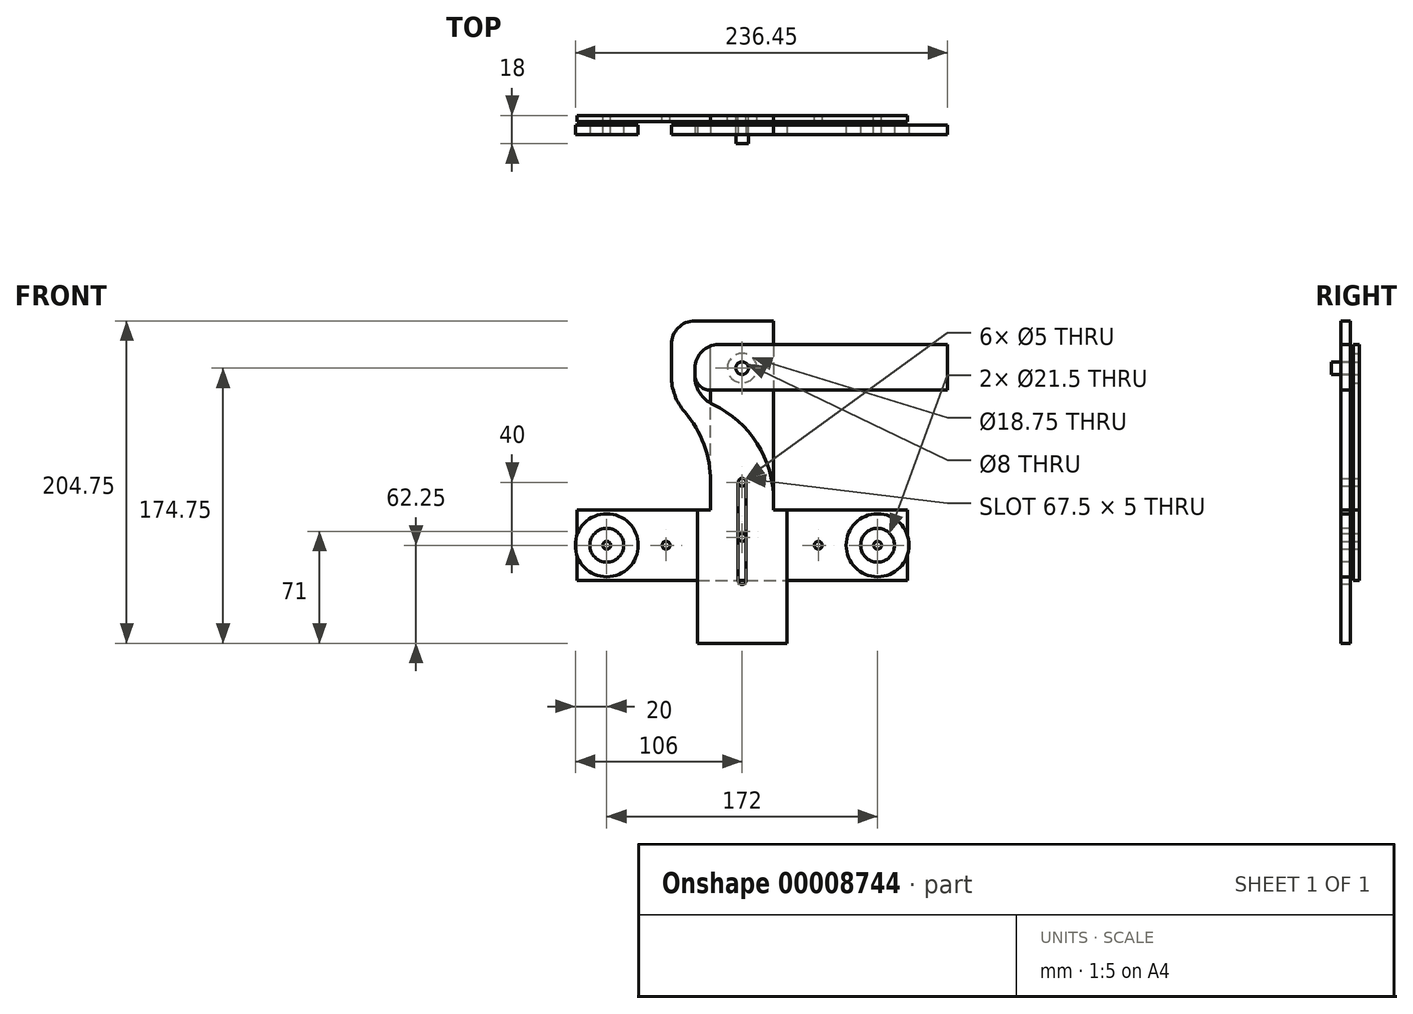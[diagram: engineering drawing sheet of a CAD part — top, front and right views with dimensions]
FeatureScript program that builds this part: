
annotation { "Feature Type Name" : "Feature", "Feature Type Description" : "" }
export const myFeature = defineFeature(function(context is Context, id is Id, definition is map)
    precondition{}
    {
        {
            var Q0;
            Q0=qCreatedBy(makeId("Front.planeOp"),FACE);
            var sketch = newSketch(context, id + "F0", { "sketchPlane" : qUnion([Q0])});
            skLineSegment(sketch, "E0", {"start": v(105, 22.5) * mm, "end": v(105, -22.5) * mm});
            skLineSegment(sketch, "E1", {"start": v(-20, 22.5) * mm, "end": v(-105, 22.5) * mm});
            skLineSegment(sketch, "E2", {"start": v(-105, -22.5) * mm, "end": v(-105, 22.5) * mm});
            skCircle(sketch, "E3", {"center": v(0, 40) * mm, "radius": 2.5 * mm});
            skLineSegment(sketch, "E4", {"start": v(-20, 112.5) * mm, "end": v(20, 112.5) * mm, "construction": true});
            skCircle(sketch, "E5", {"center": v(0, 112.5) * mm, "radius": 9.38 * mm});
            skLineSegment(sketch, "E6", {"start": v(-105, -22.5) * mm, "end": v(105, -22.5) * mm});
            skCircle(sketch, "E7", {"center": v(0, 5) * mm, "radius": 2.5 * mm});
            skCircle(sketch, "E8", {"center": v(-86, 0) * mm, "radius": 2.5 * mm});
            skCircle(sketch, "E9", {"center": v(86, 0) * mm, "radius": 2.5 * mm});
            skLineSegment(sketch, "E10", {"start": v(-20, 22.5) * mm, "end": v(20, 22.5) * mm, "construction": true});
            skLineSegment(sketch, "E11", {"start": v(0, 112.5) * mm, "end": v(0, -22.5) * mm, "construction": true});
            skLineSegment(sketch, "E12", {"start": v(-86, 0) * mm, "end": v(0, 0) * mm, "construction": true});
            skLineSegment(sketch, "E13", {"start": v(0, 0) * mm, "end": v(86, 0) * mm, "construction": true});
            skPoint(sketch, "E14", {"position": v(105, 0) * mm});
            skPoint(sketch, "E15", {"position": v(0, -22.5) * mm});
            skCircle(sketch, "E16", {"center": v(-48.35, 0) * mm, "radius": 20 * mm, "construction": true});
            skCircle(sketch, "E17", {"center": v(48.35, 0) * mm, "radius": 20 * mm, "construction": true});
            skCircle(sketch, "E18", {"center": v(-86, 0) * mm, "radius": 20 * mm, "construction": true});
            skCircle(sketch, "E19", {"center": v(86, 0) * mm, "radius": 20 * mm, "construction": true});
            skLineSegment(sketch, "E20", {"start": v(-20, 22.5) * mm, "end": v(-20, 127.5) * mm});
            skLineSegment(sketch, "E21", {"start": v(-20, 127.5) * mm, "end": v(20, 127.5) * mm});
            skLineSegment(sketch, "E22", {"start": v(20, 127.5) * mm, "end": v(20, 22.5) * mm});
            skLineSegment(sketch, "E23", {"start": v(20, 22.5) * mm, "end": v(105, 22.5) * mm});
            skCircle(sketch, "E24", {"center": v(-48.35, 0) * mm, "radius": 2.5 * mm});
            skCircle(sketch, "E25", {"center": v(48.35, 0) * mm, "radius": 2.5 * mm});
            skSolve(sketch);
        }
        {
            var Q0;
            Q0 = qSketchRegion(id + "F0", true);
            extrude(context, id + "F1", {"entities" : qUnion([Q0]), "depth" : 4 * mm});
        }
        {
            var Q0;
            Q0=makeQuery(id+"F1.opExtrude","CAP_FACE",FACE,{"disambiguationData":[OSD([sQuery(id+"F0.wireOp",EDGE,"E0"),sQuery(id+"F0.wireOp",EDGE,"b1bdffde-36e9-4f26-b447-62229c1635de"),sQuery(id+"F0.wireOp",EDGE,"6c009403-4b52-4c06-8701-ef34f8ef2d19"),sQuery(id+"F0.wireOp",EDGE,"f10999cf-903d-418b-98b1-c5591cbe51ed"),sQuery(id+"F0.wireOp",EDGE,"E1"),sQuery(id+"F0.wireOp",EDGE,"E2"),sQuery(id+"F0.wireOp",EDGE,"E3"),sQuery(id+"F0.wireOp",EDGE,"E5"),sQuery(id+"F0.wireOp",EDGE,"E6"),sQuery(id+"F0.wireOp",EDGE,"E7"),sQuery(id+"F0.wireOp",EDGE,"E8"),sQuery(id+"F0.wireOp",EDGE,"E9"),sQuery(id+"F0.wireOp",EDGE,"a64ca942-9197-43bc-8cf3-53473cfb3008"),sQuery(id+"F0.wireOp",EDGE,"94b97b06-c2ea-428e-ab4c-9c243ee04647"),sQuery(id+"F0.wireOp",EDGE,"e7d3e3b6-22b7-4308-8daa-f254cc9a82a0")])],"isStart":true});
            var sketch = newSketch(context, id + "F2", { "sketchPlane" : qUnion([Q0])});
            skCircle(sketch, "E26.0", {"center": v(0, 112.5) * mm, "radius": 4 * mm});
            skCircle(sketch, "E26.1", {"center": v(0, 40) * mm, "radius": 2.5 * mm});
            skCircle(sketch, "E26.2", {"center": v(0, 5) * mm, "radius": 2.5 * mm});
            skCircle(sketch, "E26.3", {"center": v(86, 0) * mm, "radius": 2.5 * mm});
            skCircle(sketch, "E26.4", {"center": v(-86, 0) * mm, "radius": 2.5 * mm});
            skSolve(sketch);
        }
        {
            var Q0;
            Q0 = qSketchRegion(id + "F2", true);
            extrude(context, id + "F3", {"entities" : qUnion([Q0]), "oppositeDirection" : true, "depth" : (4 * 3) * mm});
        }
        {
            var Q0;
            Q0=makeQuery(id+"F3.opExtrude","CAP_FACE",FACE,{"disambiguationData":[OSD([sQuery(id+"F2.wireOp",EDGE,"E26.0")])],"isStart":false});
            var sketch = newSketch(context, id + "F4", { "sketchPlane" : qUnion([Q0])});
            skCircle(sketch, "E27", {"center": v(-86, 0) * mm, "radius": 20 * mm});
            skCircle(sketch, "E28", {"center": v(86, 0) * mm, "radius": 20 * mm});
            skCircle(sketch, "E29", {"center": v(-86, 0) * mm, "radius": 10.75 * mm});
            skCircle(sketch, "E30", {"center": v(86, 0) * mm, "radius": 10.75 * mm});
            skSolve(sketch);
        }
        {
            var Q0;
            Q0 = qSketchRegion(id + "F4", true);
            extrude(context, id + "F5", {"entities" : qUnion([Q0]), "oppositeDirection" : true, "depth" : 6 * mm});
        }
        {
            var Q0;
            Q0=makeQuery(id+"F5.opExtrude","CAP_FACE",FACE,{"disambiguationData":[OSD([sQuery(id+"F4.wireOp",EDGE,"E27"),sQuery(id+"F4.wireOp",EDGE,"E29")])],"isStart":true});
            var sketch = newSketch(context, id + "F6", { "sketchPlane" : qUnion([Q0])});
            skArc(sketch, "E31", {"start": v(-2.5, -22.5) * mm, "mid": v(0, -25) * mm, "end": v(2.5, -22.5) * mm});
            skLineSegment(sketch, "E32", {"start": v(0, 129.3) * mm, "end": v(0, -22.5) * mm, "construction": true});
            skLineSegment(sketch, "E33", {"start": v(2.5, -22.5) * mm, "end": v(2.5, 40) * mm});
            skLineSegment(sketch, "E34", {"start": v(-2.5, -22.5) * mm, "end": v(-2.5, 40) * mm});
            skArc(sketch, "E35", {"start": v(2.5, 40) * mm, "mid": v(0, 42.5) * mm, "end": v(-2.5, 40) * mm});
            skLineSegment(sketch, "E36", {"start": v(-30, 142.5) * mm, "end": v(20, 142.5) * mm});
            skLineSegment(sketch, "E37", {"start": v(20, 142.5) * mm, "end": v(20, 127.5) * mm});
            skLineSegment(sketch, "E38", {"start": v(20, 127.5) * mm, "end": v(-15, 127.5) * mm});
            skArc(sketch, "E39.filletArc", {"start": v(-15, 127.5) * mm, "mid": v(-25.6, 123.1) * mm, "end": v(-30, 112.5) * mm});
            skArc(sketch, "E40.filletArc", {"start": v(-30, 142.5) * mm, "mid": v(-40.6, 138.1) * mm, "end": v(-45, 127.5) * mm});
            skLineSegment(sketch, "E41", {"start": v(-45, 127.5) * mm, "end": v(-45, 107.5) * mm});
            skLineSegment(sketch, "E42", {"start": v(-20, 40.5) * mm, "end": v(-20, 22.5) * mm});
            skLineSegment(sketch, "E43", {"start": v(-20, 22.5) * mm, "end": v(-28.35, 22.5) * mm});
            skLineSegment(sketch, "E44", {"start": v(-28.35, 22.5) * mm, "end": v(-28.35, -62.25) * mm});
            skLineSegment(sketch, "E45", {"start": v(-28.35, -62.25) * mm, "end": v(28.35, -62.25) * mm});
            skLineSegment(sketch, "E46", {"start": v(28.35, -62.25) * mm, "end": v(28.35, 22.5) * mm});
            skLineSegment(sketch, "E47", {"start": v(28.35, 22.5) * mm, "end": v(20, 22.5) * mm});
            skLineSegment(sketch, "E48", {"start": v(20, 22.5) * mm, "end": v(20, 28.58) * mm});
            skLineSegment(sketch, "E49", {"start": v(-30, 107.5) * mm, "end": v(-30, 112.5) * mm});
            skPoint(sketch, "E50.visualSharp", {"position": v(-30, 87.5) * mm});
            skArc(sketch, "E50.filletArc", {"start": v(-30, 107.5) * mm, "mid": v(-26.9, 96.8) * mm, "end": v(-18.54, 89.42) * mm});
            skArc(sketch, "E51.0", {"start": v(-45, 107.5) * mm, "mid": v(-42.8, 95.26) * mm, "end": v(-36.45, 84.57) * mm});
            skPoint(sketch, "E52.visualSharp", {"position": v(20, 87.5) * mm});
            skArc(sketch, "E52.filletArc", {"start": v(20, 28.58) * mm, "mid": v(9.55, 64.59) * mm, "end": v(-18.54, 89.42) * mm});
            skPoint(sketch, "E53.visualSharp", {"position": v(-20, 73.96) * mm});
            skArc(sketch, "E53.filletArc", {"start": v(-20, 40.5) * mm, "mid": v(-24.25, 64.02) * mm, "end": v(-36.45, 84.57) * mm});
            skSolve(sketch);
        }
        {
            var Q0;
            Q0 = qSketchRegion(id + "F6", true);
            extrude(context, id + "F7", {"entities" : qUnion([Q0]), "oppositeDirection" : true, "depth" : 6 * mm});
        }
        {
            var Q0;
            Q0=makeQuery(id+"F3.opExtrude","CAP_FACE",FACE,{"disambiguationData":[OSD([sQuery(id+"F2.wireOp",EDGE,"E26.0")])],"isStart":false});
            var sketch = newSketch(context, id + "F8", { "sketchPlane" : qUnion([Q0])});
            skCircle(sketch, "E54.0", {"center": v(0, 112.5) * mm, "radius": 4 * mm});
            skSolve(sketch);
        }
        {
            var Q0;
            Q0 = qSketchRegion(id + "F8", true);
            extrude(context, id + "F9", {"entities" : qUnion([Q0]), "operationType" : NewBodyOperationType.ADD, "depth" : 6 * mm});
        }
        {
            var Q0;
            Q0=makeQuery(id+"F7.opExtrude","CAP_FACE",FACE,{"disambiguationData":[OSD([sQuery(id+"F6.wireOp",EDGE,"7a91dfa8-aa92-46c7-8a28-5e4d083e5be4"),sQuery(id+"F6.wireOp",EDGE,"5f1317f1-af8d-4f90-87c7-87565ad7c9fc"),sQuery(id+"F6.wireOp",EDGE,"5eaf847d-071f-4fab-925d-528e8d7daa96"),sQuery(id+"F6.wireOp",EDGE,"9496637e-6192-491a-bce5-487fc87408d0"),sQuery(id+"F6.wireOp",EDGE,"d388f8b3-3bed-4612-a944-b0fa34927e18"),sQuery(id+"F6.wireOp",EDGE,"e9fc0810-f8fe-413a-a931-e83ffce41a42"),sQuery(id+"F6.wireOp",EDGE,"770771a2-f9db-4e4c-958d-0db291cef076"),sQuery(id+"F6.wireOp",EDGE,"6d283ee7-ce5c-42f6-b5ae-b53ba640d1a3"),sQuery(id+"F6.wireOp",EDGE,"a378780b-862b-4f98-991a-37073ba94121"),sQuery(id+"F6.wireOp",EDGE,"72654bc0-8fd7-47ab-9f3f-13cce299ab59"),sQuery(id+"F6.wireOp",EDGE,"7837c3cb-c515-43e7-a355-5ca101961bf5"),sQuery(id+"F6.wireOp",EDGE,"fa5a5b3e-309f-437b-a5d9-4479115bd696"),sQuery(id+"F6.wireOp",EDGE,"92dbf227-37e1-4007-b594-be1603488aa9"),sQuery(id+"F6.wireOp",EDGE,"E31"),sQuery(id+"F6.wireOp",EDGE,"ebb9432c-e0c9-4ad6-bef2-6b251fc06809"),sQuery(id+"F6.wireOp",EDGE,"e0b87db3-ea4e-4707-8de5-01d7d0488b13.filletArc"),sQuery(id+"F6.wireOp",EDGE,"08dfe0e6-7c46-43a5-a4bb-0d35a965ed27.filletArc"),sQuery(id+"F6.wireOp",EDGE,"bdcb1b2e-ac5c-4d20-8f3c-43608db35e52.filletArc"),sQuery(id+"F6.wireOp",EDGE,"8b2f8c48-9b0d-4b66-9ca6-4adea88158e0.filletArc"),sQuery(id+"F6.wireOp",EDGE,"E33"),sQuery(id+"F6.wireOp",EDGE,"E34"),sQuery(id+"F6.wireOp",EDGE,"E35"),sQuery(id+"F6.wireOp",EDGE,"b75bc95b-5d8b-46b1-b6af-f629cbc22cf3")])],"isStart":true});
            var sketch = newSketch(context, id + "F10", { "sketchPlane" : qUnion([Q0])});
            skLineSegment(sketch, "E55", {"start": v(130.45, 98.5) * mm, "end": v(130.45, 127.5) * mm});
            skCircle(sketch, "E56.0", {"center": v(0, 112.5) * mm, "radius": 4 * mm});
            skLineSegment(sketch, "E57", {"start": v(130.45, 98.5) * mm, "end": v(-20, 98.5) * mm});
            skLineSegment(sketch, "E58", {"start": v(-30, 108.5) * mm, "end": v(-30, 112.5) * mm});
            skLineSegment(sketch, "E59", {"start": v(-15, 127.5) * mm, "end": v(130.45, 127.5) * mm});
            skPoint(sketch, "E60.visualSharp", {"position": v(-30, 127.5) * mm});
            skArc(sketch, "E60.filletArc", {"start": v(-15, 127.5) * mm, "mid": v(-25.6, 123.1) * mm, "end": v(-30, 112.5) * mm});
            skPoint(sketch, "E61.visualSharp", {"position": v(-30, 98.5) * mm});
            skArc(sketch, "E61.filletArc", {"start": v(-30, 108.5) * mm, "mid": v(-27.07, 101.43) * mm, "end": v(-20, 98.5) * mm});
            skCircle(sketch, "E62", {"center": v(0, 112.5) * mm, "radius": 14 * mm, "construction": true});
            skSolve(sketch);
        }
        {
            var Q0;
            Q0 = qSketchRegion(id + "F10", true);
            extrude(context, id + "F11", {"entities" : qUnion([Q0]), "oppositeDirection" : true, "depth" : 6 * mm});
        }
    });
